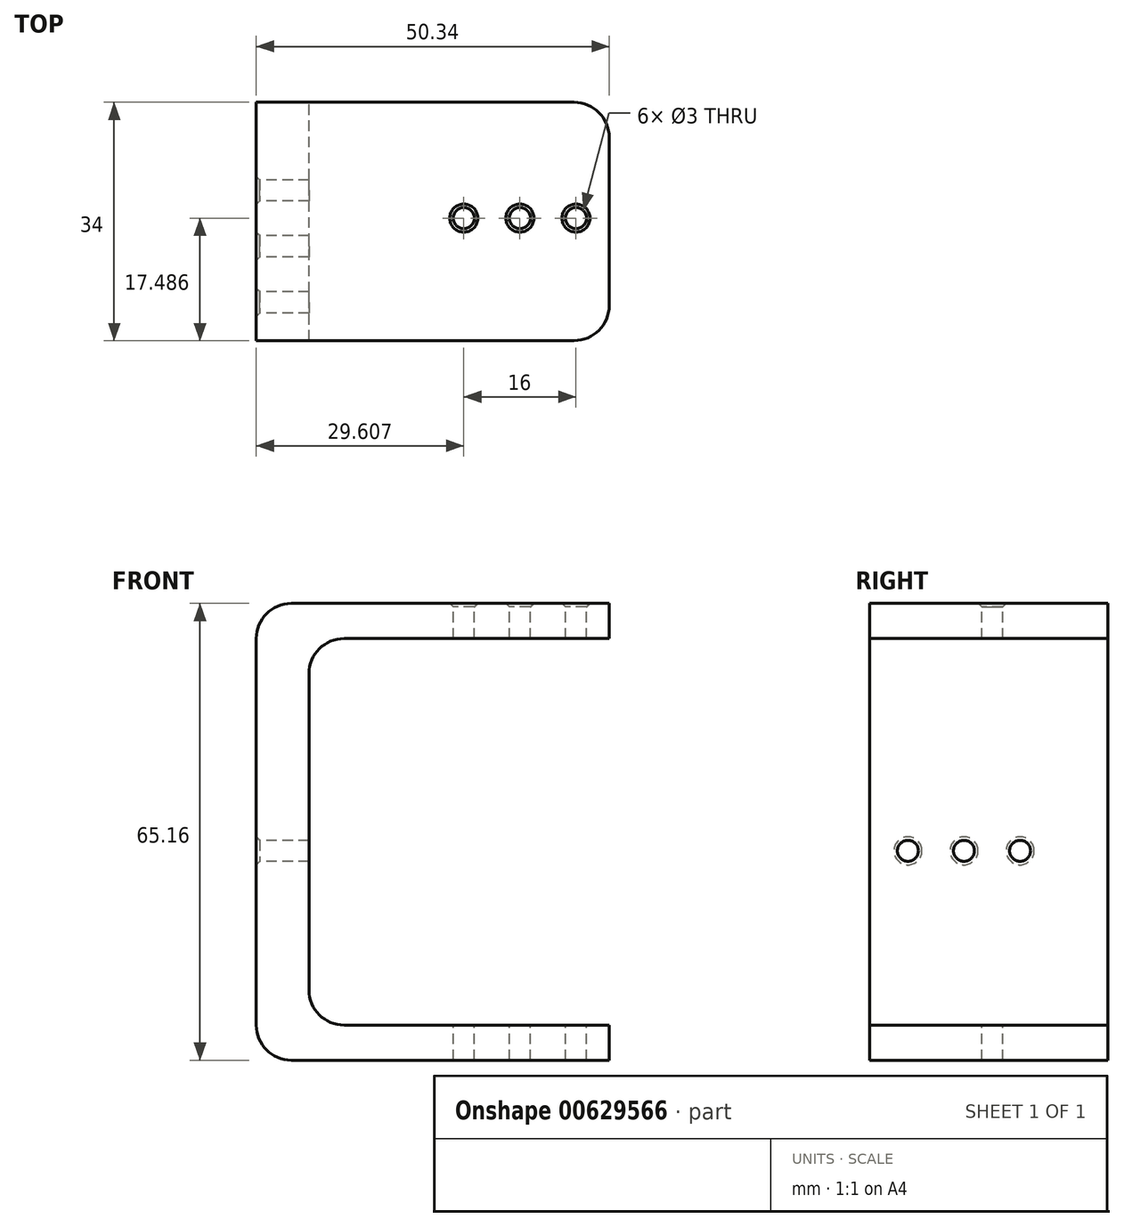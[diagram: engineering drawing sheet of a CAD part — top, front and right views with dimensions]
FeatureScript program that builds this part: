
annotation { "Feature Type Name" : "Feature", "Feature Type Description" : "" }
export const myFeature = defineFeature(function(context is Context, id is Id, definition is map)
    precondition{}
    {
        {
            var Q0;
            Q0=qCreatedBy(makeId("Front.planeOp"),FACE);
            var sketch = newSketch(context, id + "F0", { "sketchPlane" : qUnion([Q0])});
            skLineSegment(sketch, "E0", {"start": v(-37.96, 35.29) * mm, "end": v(-37.96, -29.87) * mm});
            skLineSegment(sketch, "E1", {"start": v(-37.96, 35.29) * mm, "end": v(12.38, 35.29) * mm});
            skLineSegment(sketch, "E2", {"start": v(-37.96, -29.87) * mm, "end": v(12.38, -29.87) * mm});
            skLineSegment(sketch, "E3", {"start": v(12.38, -29.87) * mm, "end": v(12.38, -24.87) * mm});
            skLineSegment(sketch, "E4", {"start": v(12.38, -24.87) * mm, "end": v(-30.42, -24.87) * mm});
            skLineSegment(sketch, "E5", {"start": v(-30.42, -24.87) * mm, "end": v(-30.42, -29.87) * mm});
            skLineSegment(sketch, "E6", {"start": v(-30.42, -29.87) * mm, "end": v(-30.42, -24.87) * mm});
            skLineSegment(sketch, "E7", {"start": v(-30.42, 35.29) * mm, "end": v(-30.42, -24.87) * mm});
            skLineSegment(sketch, "E8", {"start": v(-30.42, 30.29) * mm, "end": v(12.38, 30.29) * mm});
            skLineSegment(sketch, "E9", {"start": v(12.38, 30.29) * mm, "end": v(12.38, 35.29) * mm});
            skSolve(sketch);
        }
        {
            var Q0;
            Q0 = qSketchRegion(id + "F0", true);
            extrude(context, id + "F1", {"entities" : qUnion([Q0]), "depth" : 34 * mm, "offsetDistance" : 25 * mm});
        }
        {
            var Q0;
            Q0=makeQuery(id+"F1.opExtrude","CAP_EDGE",EDGE,{"disambiguationData":[OSD([sQuery(id+"F0.wireOp",EDGE,"E9")])],"isStart":false});
            fillet(context, id + "F2", {"entities" : qUnion([Q0]), "radius" : 5 * mm, "tangentPropagation" : true, "allowEdgeOverflow" : false});
        }
        {
            var Q0;
            Q0=makeQuery(id+"F1.opExtrude","CAP_EDGE",EDGE,{"disambiguationData":[OSD([sQuery(id+"F0.wireOp",EDGE,"E9")])],"isStart":true});
            fillet(context, id + "F3", {"entities" : qUnion([Q0]), "radius" : 5 * mm, "tangentPropagation" : true, "allowEdgeOverflow" : false});
        }
        {
            var Q0;
            Q0=makeQuery(id+"F1.opExtrude","CAP_EDGE",EDGE,{"disambiguationData":[OSD([sQuery(id+"F0.wireOp",EDGE,"E3")])],"isStart":false});
            fillet(context, id + "F4", {"entities" : qUnion([Q0]), "radius" : 5 * mm, "tangentPropagation" : true, "allowEdgeOverflow" : false});
        }
        {
            var Q0;
            Q0=makeQuery(id+"F1.opExtrude","CAP_EDGE",EDGE,{"disambiguationData":[OSD([sQuery(id+"F0.wireOp",EDGE,"E3")])],"isStart":true});
            fillet(context, id + "F5", {"entities" : qUnion([Q0]), "radius" : 5 * mm, "tangentPropagation" : true, "allowEdgeOverflow" : false});
        }
        {
            var Q0;
            Q0=makeQuery(id+"F1.opExtrude","SWEPT_EDGE",EDGE,{"disambiguationData":[OSD([sQuery(id+"F0.wireOp",EDGE,"E0"),sQuery(id+"F0.wireOp",EDGE,"E1")])]});
            fillet(context, id + "F6", {"entities" : qUnion([Q0]), "radius" : 5 * mm, "tangentPropagation" : true, "allowEdgeOverflow" : false});
        }
        {
            var Q0;
            Q0=makeQuery(id+"F1.opExtrude","SWEPT_EDGE",EDGE,{"disambiguationData":[OSD([sQuery(id+"F0.wireOp",EDGE,"E4"),sQuery(id+"F0.wireOp",EDGE,"E6"),sQuery(id+"F0.wireOp",EDGE,"E7")])]});
            var Q1;
            Q1=makeQuery(id+"F1.opExtrude","SWEPT_EDGE",EDGE,{"disambiguationData":[OSD([sQuery(id+"F0.wireOp",EDGE,"E7"),sQuery(id+"F0.wireOp",EDGE,"E8")])]});
            var Q2;
            Q2=makeQuery(id+"F1.opExtrude","SWEPT_EDGE",EDGE,{"disambiguationData":[OSD([sQuery(id+"F0.wireOp",EDGE,"E0"),sQuery(id+"F0.wireOp",EDGE,"E2")])]});
            fillet(context, id + "F7", {"entities" : qUnion([Q0, Q1, Q2]), "radius" : 5 * mm, "tangentPropagation" : true, "allowEdgeOverflow" : false});
        }
        {
            var Q0;
            Q0=makeQuery(id+"F1.opExtrude","SWEPT_FACE",FACE,{"disambiguationData":[OSD([sQuery(id+"F0.wireOp",EDGE,"E1")])]});
            var sketch = newSketch(context, id + "F8", { "sketchPlane" : qUnion([Q0])});
            skCircle(sketch, "E10", {"center": v(-8.35, -16.51) * mm, "radius": 0.75 * mm});
            skCircle(sketch, "E11.1.0.0", {"center": v(-0.35, -16.51) * mm, "radius": 0.75 * mm});
            skCircle(sketch, "E11.2.0.0", {"center": v(7.65, -16.51) * mm, "radius": 0.75 * mm});
            skSolve(sketch);
        }
        {
            var Q0;
            Q0=makeQuery(id+"F1.opExtrude","SWEPT_FACE",FACE,{"disambiguationData":[OSD([sQuery(id+"F0.wireOp",EDGE,"E0")])]});
            var sketch = newSketch(context, id + "F9", { "sketchPlane" : qUnion([Q0])});
            skCircle(sketch, "E12", {"center": v(12.55, 0) * mm, "radius": 0.75 * mm});
            skCircle(sketch, "E13.1.0.0", {"center": v(20.55, 0) * mm, "radius": 0.75 * mm});
            skCircle(sketch, "E13.2.0.0", {"center": v(28.55, 0) * mm, "radius": 0.75 * mm});
            skSolve(sketch);
        }
        {
            var Q0;
            Q0=sQuery(id+"F9.wireOp",VERTEX,"E12.center");
            var Q1;
            Q1=sQuery(id+"F9.wireOp",VERTEX,"E13.1.0.0.center");
            var Q2;
            Q2=sQuery(id+"F9.wireOp",VERTEX,"E13.2.0.0.center");
            var Q3;
            Q3=makeQuery(id+"F1.opExtrude","SWEPT_BODY",BODY,{"disambiguationData":[OSD([sQuery(id+"F0.wireOp",EDGE,"E0"),sQuery(id+"F0.wireOp",EDGE,"E1"),sQuery(id+"F0.wireOp",EDGE,"E2"),sQuery(id+"F0.wireOp",EDGE,"E3"),sQuery(id+"F0.wireOp",EDGE,"E4"),sQuery(id+"F0.wireOp",EDGE,"E7"),sQuery(id+"F0.wireOp",EDGE,"E8"),sQuery(id+"F0.wireOp",EDGE,"E9")])]});
            hole(context, id + "F10", {"style" : HoleStyle.C_SINK, "endStyle" : HoleEndStyle.THROUGH, "holeDiameter" : 3 * mm, "cSinkDiameter" : 4 * mm, "cSinkAngle" : 90 * degree, "majorDiameter" : 5 * mm, "isTappedThrough" : true, "tappedDepth" : 12 * mm, "tapClearance" : 3, "locations" : qUnion([Q0, Q1, Q2]), "scope" : qUnion([Q3])});
        }
        {
            var Q0;
            Q0=sQuery(id+"F8.wireOp",VERTEX,"E11.1.0.0.center");
            var Q1;
            Q1=sQuery(id+"F8.wireOp",VERTEX,"E10.center");
            var Q2;
            Q2=sQuery(id+"F8.wireOp",VERTEX,"E11.2.0.0.center");
            var Q3;
            Q3=makeQuery(id+"F1.opExtrude","SWEPT_BODY",BODY,{"disambiguationData":[OSD([sQuery(id+"F0.wireOp",EDGE,"E0"),sQuery(id+"F0.wireOp",EDGE,"E1"),sQuery(id+"F0.wireOp",EDGE,"E2"),sQuery(id+"F0.wireOp",EDGE,"E3"),sQuery(id+"F0.wireOp",EDGE,"E4"),sQuery(id+"F0.wireOp",EDGE,"E7"),sQuery(id+"F0.wireOp",EDGE,"E8"),sQuery(id+"F0.wireOp",EDGE,"E9")])]});
            hole(context, id + "F11", {"style" : HoleStyle.C_SINK, "endStyle" : HoleEndStyle.THROUGH, "holeDiameter" : 3 * mm, "cSinkDiameter" : 4 * mm, "cSinkAngle" : 90 * degree, "majorDiameter" : 5 * mm, "isTappedThrough" : true, "tappedDepth" : 12 * mm, "tapClearance" : 3, "locations" : qUnion([Q0, Q1, Q2]), "scope" : qUnion([Q3])});
        }
    });
